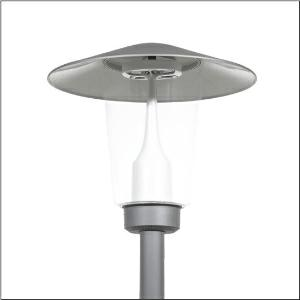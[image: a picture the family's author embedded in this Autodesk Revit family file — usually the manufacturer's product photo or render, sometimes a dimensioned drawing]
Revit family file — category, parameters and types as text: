
# Revit family: pilzleuchte_iq___st1_2a_5xa5235af14h_f6cb
name_source: partatom
category: Lighting Fixtures
units: mm (PartAtom-declared; Revit-internal decimal feet)

## family parameters
Cut with Voids When Loaded = No
Host = Face
Light Source = No
Part Type = Normal
Room Calculation Point = No
Round Connector Dimension = Use Diameter
Shared = No

## types (1)
- --- (1 x LED, 1550 lm, 12.9 W, 2200K)
    Apparent Load = 13 VA
    CIE Flux Codes = 24 61 93 98 100
    Color Rendering = 70
    Color Temperature = 2200K
    Default Elevation = 1800 mm
    Description = Mushroom Luminaire iQ, mast luminaire, Module 540 iQ-SR, primary light control with 3 zone facetted reflector, of plastic, silver coated, highly specular, structured, primary optical cover: cover, of PMMA, transparent, light distribution: ST1.2a, light emission: direct distribution, primary light characteristic: asymmetric, installation type: post-top, LED, High Power LED, rated luminous flux: 1.550lm, luminous efficacy: 120lm/W, light colour: 722, colour temperature: 2200K, control gear: ECG iQ, control: presetting dimming logarithmic, Street-Remote, Auto-Match, Temp-Guard, Lumen-Switch, Night-Set, Smart-Wire, Light-Fading, Desk-Remote (wireless, voltage-free reading and setting of iQ features in the workshop via application-optimized NFC function/RFID function), optimised constant luminous flux control (CLO 2.0), with terminal, 6-pole, max. 2.5mm², mains connection: 230..240V, AC, 50/60Hz, start of lifetime: 13W, end of service life: 13W, reduction: 6W, luminaire housing, upper part, of glass-fibre reinforced polyester, coated, Siteco® metallic grey (DB 702S), diameter: 650mm, height: 586mm, spigot size: d x l = 76 x 70mm (post-top) | with reducer (optional accessory) 60 x 70mm, post-top mast mounting element, of diecast aluminium, coated, Siteco® metallic grey (DB 702S), Module 540 iQ-SR, traffic white (RAL 9016), equipment: standard, protection rating (complete): IP65, insulation class (complete): insulation class II (safety insulation), certification: CE, ENEC, VDE, packaging unit: 1 piece

Light Distribution: ST1.2a
    Height = 586 mm
    Lamp = 1 x LED
    Lamp Light Flux = 1550 lm
    Lamp Power = 12.9 W
    Lamp count = 1
    Length = 650 mm
    Luminous efficacy = 120 lm/W
    Manufacturer = Siteco
    ModVariant = No
    Model = 5XA5235AF14H
    Number of Poles = 1
    OnlyDefault = Yes
    Power Factor = 1
    Product Name = Pilzleuchte iQ | ST1.2a
    Product group = mast luminaire | pylon top
    ProductGroupID = 6100
    Protection Class = Protection class II
    Protection Degree = IP 65
    RLX_Detail_Level = 1
    RLX_Emergency_Light_Flux = 0 lm
    RLX_Emergency_Type = 0
    RLX_Emergency_Type_DB = No
    RlxData = <blob elided: 124329 chars, md5=8b90e1c0>
    Socket = socket
    Standby Power = 0 W
    System Light Flux = 1550 lm
    System Power = 13 W
    Type Comments = factory setting: luminous flux: 100 % | dim-lin: 254 | 516 mA
    Type Image = l_1006077.jpg
    URL = http://relux.com
    VarID = @adj_110973
    Voltage = 0 V
    Weight = 0.00 kg
    Width = 0 mm  [stored 0 ft]

note: [stored X ft] marks values corroborated as IEEE doubles in the binary element streams (Revit-internal decimal feet)

## geometry (parser evidence)
native form markers: Blend x4, Sweep x9
no freeform markers — native parametric forms only
